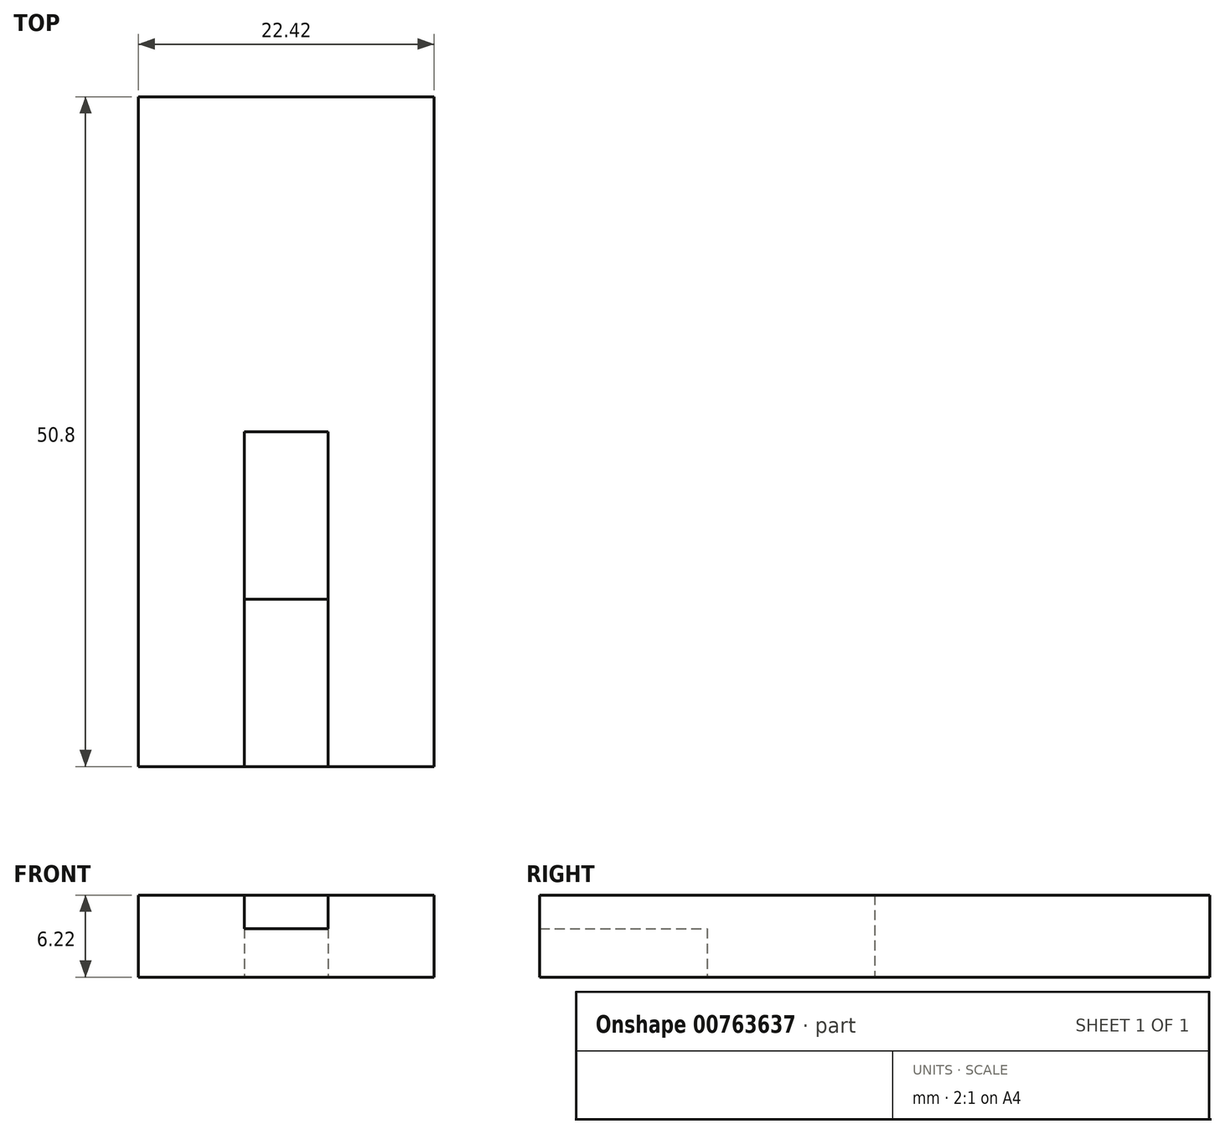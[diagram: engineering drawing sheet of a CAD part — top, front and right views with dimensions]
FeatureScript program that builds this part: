
annotation { "Feature Type Name" : "Feature", "Feature Type Description" : "" }
export const myFeature = defineFeature(function(context is Context, id is Id, definition is map)
    precondition{}
    {
        {
            var Q0;
            Q0=qCreatedBy(makeId("Top.planeOp"),FACE);
            var sketch = newSketch(context, id + "F0", { "sketchPlane" : qUnion([Q0])});
            skLineSegment(sketch, "E0.bottom", {"start": v(11.21, -25.4) * mm, "end": v(-11.21, -25.4) * mm});
            skLineSegment(sketch, "E0.top", {"start": v(11.21, 25.4) * mm, "end": v(-11.21, 25.4) * mm});
            skLineSegment(sketch, "E0.left", {"start": v(11.21, -25.4) * mm, "end": v(11.21, 25.4) * mm});
            skLineSegment(sketch, "E0.right", {"start": v(-11.21, -25.4) * mm, "end": v(-11.21, 25.4) * mm});
            skPoint(sketch, "E0.middle", {"position": v(0, 0) * mm});
            skLineSegment(sketch, "E1.bottom", {"start": v(-3.17, -25.4) * mm, "end": v(3.17, -25.4) * mm});
            skLineSegment(sketch, "E1.top", {"start": v(-3.17, 0) * mm, "end": v(3.17, 0) * mm});
            skLineSegment(sketch, "E1.left", {"start": v(-3.18, -25.4) * mm, "end": v(-3.17, 0) * mm});
            skLineSegment(sketch, "E1.right", {"start": v(3.17, -25.4) * mm, "end": v(3.18, 0) * mm});
            skLineSegment(sketch, "E2", {"start": v(-3.18, -12.7) * mm, "end": v(3.18, -12.7) * mm});
            skSolve(sketch);
        }
        {
            var Q0;
            Q0=makeQuery(id+"F0.imprint","IMPRINT",FACE,{"disambiguationData":[TD([[makeQuery(id+"F0.imprint","IMPRINT",EDGE,{"derivedFrom":sQuery(id+"F0.wireOp",EDGE,"E0.top")}),1.0]])]});
            extrude(context, id + "F1", {"entities" : qUnion([Q0]), "depth" : 6.22 * mm, "offsetDistance" : 25.4 * mm});
        }
        {
            var Q0;
            {var subQ5=sQuery(id+"F0.wireOp",EDGE,"E2");Q0=makeQuery(id+"F0.imprint","IMPRINT",FACE,{"disambiguationData":[TD([[makeQuery(id+"F0.imprint","IMPRINT",EDGE,{"derivedFrom":subQ5}),-1.0]])]});}
            extrude(context, id + "F2", {"entities" : qUnion([Q0]), "operationType" : NewBodyOperationType.ADD, "depth" : 3.68 * mm, "offsetDistance" : 25.4 * mm});
        }
    });
